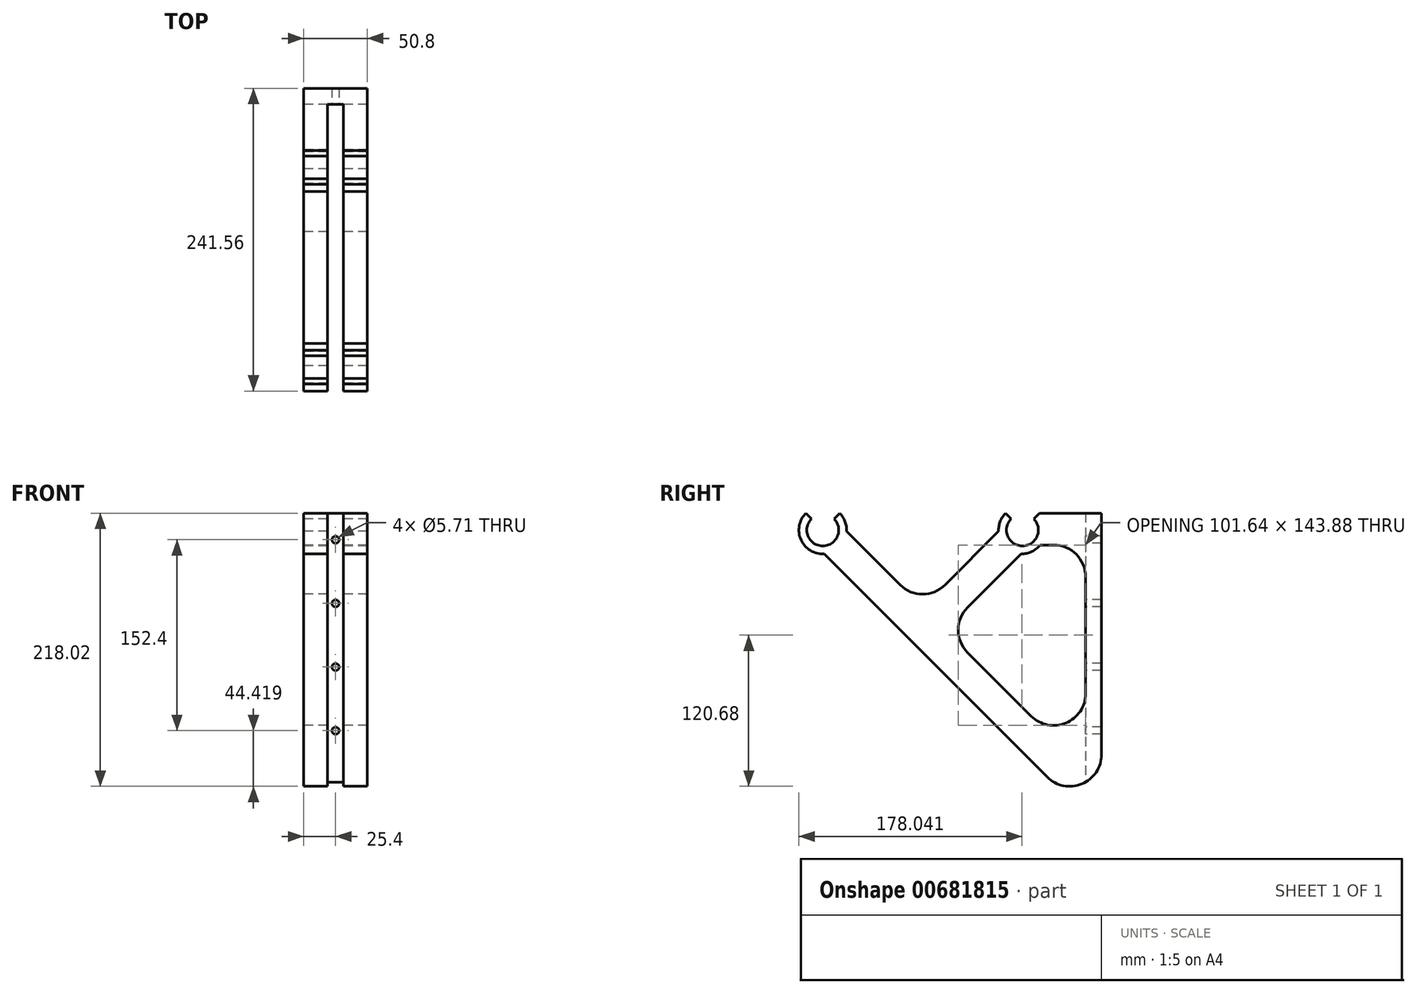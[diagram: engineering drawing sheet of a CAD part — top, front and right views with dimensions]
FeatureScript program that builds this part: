
annotation { "Feature Type Name" : "Feature", "Feature Type Description" : "" }
export const myFeature = defineFeature(function(context is Context, id is Id, definition is map)
    precondition{}
    {
        {
            var Q0;
            Q0=qCreatedBy(makeId("Right.planeOp"),FACE);
            var sketch = newSketch(context, id + "F0", { "sketchPlane" : qUnion([Q0])});
            skCircle(sketch, "E0", {"center": v(0, 0) * mm, "radius": 100 * mm});
            skLineSegment(sketch, "E1", {"start": v(0, 0) * mm, "end": v(0, -100) * mm});
            skLineSegment(sketch, "E2", {"start": v(0, 0) * mm, "end": v(70.71, -70.71) * mm});
            skLineSegment(sketch, "E3.MirrorCS", {"start": v(0, 0) * mm, "end": v(-70.71, -70.71) * mm});
            skCircle(sketch, "E4", {"center": v(79.7, -79.7) * mm, "radius": 12.7 * mm});
            skLineSegment(sketch, "E5", {"start": v(79.7, -79.7) * mm, "end": v(79.7, -67) * mm});
            skLineSegment(sketch, "E6", {"start": v(79.7, -79.7) * mm, "end": v(70.71, -70.71) * mm});
            skCircle(sketch, "E7.MirrorC", {"center": v(-79.7, -79.7) * mm, "radius": 12.7 * mm});
            skArc(sketch, "E8.0", {"start": v(-66.22, -66.22) * mm, "mid": v(-61.9, -72.9) * mm, "end": v(-60.67, -80.75) * mm});
            skLineSegment(sketch, "E9", {"start": v(-79.7, -79.7) * mm, "end": v(-79.7, -67) * mm});
            skLineSegment(sketch, "E10", {"start": v(-79.7, -79.7) * mm, "end": v(-93.16, -66.22) * mm});
            skLineSegment(sketch, "E11.MirrorCS", {"start": v(-79.7, -79.7) * mm, "end": v(-66.22, -66.22) * mm});
            skLineSegment(sketch, "E12.MirrorCS", {"start": v(79.7, -79.7) * mm, "end": v(66.22, -66.22) * mm});
            skLineSegment(sketch, "E13.MirrorCS", {"start": v(79.7, -79.7) * mm, "end": v(93.16, -66.22) * mm});
            skArc(sketch, "E14.trimOffspring", {"start": v(-79.7, -60.64) * mm, "mid": v(-79.6, -60.64) * mm, "end": v(-79.51, -60.64) * mm});
            skLineSegment(sketch, "E15", {"start": v(142.82, -66.22) * mm, "end": v(142.82, -258.84) * mm});
            skLineSegment(sketch, "E16.0", {"start": v(-78.63, -98.71) * mm, "end": v(99.46, -276.8) * mm});
            skLineSegment(sketch, "E17.0", {"start": v(-60.67, -80.75) * mm, "end": v(-17.96, -123.46) * mm});
            skLineSegment(sketch, "E18", {"start": v(142.82, -66.22) * mm, "end": v(130.12, -66.22) * mm});
            skLineSegment(sketch, "E19.0", {"start": v(93.89, -91.62) * mm, "end": v(104.72, -91.62) * mm});
            skLineSegment(sketch, "E20.0", {"start": v(78.63, -98.71) * mm, "end": v(35.92, -141.42) * mm});
            skLineSegment(sketch, "E21.0", {"start": v(60.67, -80.75) * mm, "end": v(17.96, -123.46) * mm});
            skArc(sketch, "E22.trimOffspring", {"start": v(60.67, -80.75) * mm, "mid": v(61.9, -72.9) * mm, "end": v(66.22, -66.22) * mm});
            skLineSegment(sketch, "E23.trimOffspring", {"start": v(35.92, -177.34) * mm, "end": v(86.76, -228.18) * mm});
            skArc(sketch, "E24.trimOffspring", {"start": v(-78.63, -98.71) * mm, "mid": v(-97.08, -87.47) * mm, "end": v(-93.16, -66.22) * mm});
            skArc(sketch, "E25.trimOffspring", {"start": v(93.89, -91.62) * mm, "mid": v(87.09, -96.94) * mm, "end": v(78.63, -98.71) * mm});
            skLineSegment(sketch, "E26.trimOffspring", {"start": v(130.12, -117.02) * mm, "end": v(130.12, -210.22) * mm});
            skLineSegment(sketch, "E27", {"start": v(93.16, -66.22) * mm, "end": v(130.12, -66.22) * mm});
            skPoint(sketch, "E28.visualSharp", {"position": v(0, -141.42) * mm});
            skArc(sketch, "E28.filletArc", {"start": v(-17.96, -123.46) * mm, "mid": v(0, -130.9) * mm, "end": v(17.96, -123.46) * mm});
            skPoint(sketch, "E29.visualSharp", {"position": v(17.96, -159.38) * mm});
            skArc(sketch, "E29.filletArc", {"start": v(35.92, -141.42) * mm, "mid": v(28.48, -159.38) * mm, "end": v(35.92, -177.34) * mm});
            skPoint(sketch, "E30.visualSharp", {"position": v(130.12, -91.62) * mm});
            skArc(sketch, "E30.filletArc", {"start": v(130.12, -117.02) * mm, "mid": v(122.68, -99.06) * mm, "end": v(104.72, -91.62) * mm});
            skPoint(sketch, "E31.visualSharp", {"position": v(130.12, -271.54) * mm});
            skArc(sketch, "E31.filletArc", {"start": v(86.76, -228.18) * mm, "mid": v(114.44, -233.69) * mm, "end": v(130.12, -210.22) * mm});
            skPoint(sketch, "E32.visualSharp", {"position": v(142.82, -320.16) * mm});
            skArc(sketch, "E32.filletArc", {"start": v(99.46, -276.8) * mm, "mid": v(127.14, -282.3) * mm, "end": v(142.82, -258.84) * mm});
            skSolve(sketch);
        }
        {
            var Q0;
            Q0=makeQuery(id+"F0.imprint","IMPRINT",FACE,{"disambiguationData":[TD([[makeQuery(id+"F0.imprint","IMPRINT",EDGE,{"derivedFrom":sQuery(id+"F0.wireOp",EDGE,"E15")}),-1.0]])]});
            var Q1;
            {var subQ0=sQuery(id+"F0.wireOp",EDGE,"E22.trimOffspring");var subQ1=sQuery(id+"F0.wireOp",EDGE,"E0");var subQ2=makeQuery(id+"F0.imprint","INTERSECT",VERTEX,{"derivedFrom":[subQ1,subQ0]});Q1=makeQuery(id+"F0.imprint","IMPRINT",FACE,{"disambiguationData":[TD([[makeQuery(id+"F0.imprint","IMPRINT",EDGE,{"disambiguationData":[TD([[subQ2,-1.0]])],"derivedFrom":subQ1}),1.0]])]});}
            var Q2;
            {var subQ0=sQuery(id+"F0.wireOp",EDGE,"E8.0");var subQ1=sQuery(id+"F0.wireOp",EDGE,"E0");var subQ2=makeQuery(id+"F0.imprint","INTERSECT",VERTEX,{"derivedFrom":[subQ1,subQ0]});Q2=makeQuery(id+"F0.imprint","IMPRINT",FACE,{"disambiguationData":[TD([[makeQuery(id+"F0.imprint","IMPRINT",EDGE,{"disambiguationData":[TD([[subQ2,1.0]])],"derivedFrom":subQ1}),1.0]])]});}
            extrude(context, id + "F1", {"entities" : qUnion([Q0, Q1, Q2]), "depth" : 50.8 * mm, "offsetDistance" : 25.4 * mm});
        }
        {
            var Q0;
            Q0=makeQuery(id+"F1.opExtrude","SWEPT_FACE",FACE,{"disambiguationData":[OSD([sQuery(id+"F0.wireOp",EDGE,"E26.trimOffspring")])]});
            cPlane(context, id + "F2", {"entities" : qUnion([Q0]), "cplaneType" : CPlaneType.OFFSET, "offset" : 254 * mm, "width" : 152.4 * mm, "height" : 152.4 * mm});
        }
        {
            var Q0;
            Q0=qCreatedBy(id+"F2.planeOp",FACE);
            var sketch = newSketch(context, id + "F3", { "sketchPlane" : qUnion([Q0])});
            skLineSegment(sketch, "E33.0", {"start": v(50.8, -66.22) * mm, "end": v(0, -66.22) * mm});
            skLineSegment(sketch, "E34", {"start": v(50.8, -284.24) * mm, "end": v(0, -284.24) * mm});
            skLineSegment(sketch, "E35", {"start": v(31.75, -66.22) * mm, "end": v(31.75, -284.24) * mm});
            skLineSegment(sketch, "E36", {"start": v(19.05, -66.22) * mm, "end": v(19.05, -284.24) * mm});
            skSolve(sketch);
        }
        {
            var Q0;
            Q0 = qSketchRegion(id + "F3", true);
            var Q1;
            Q1=makeQuery(id+"F1.opExtrude","SWEPT_FACE",FACE,{"disambiguationData":[OSD([sQuery(id+"F0.wireOp",EDGE,"E26.trimOffspring")])]});
            extrude(context, id + "F4", {"entities" : qUnion([Q0]), "operationType" : NewBodyOperationType.REMOVE, "endBound" : BoundingType.UP_TO_SURFACE, "oppositeDirection" : true, "depth" : 25.4 * mm, "endBoundEntityFace" : qUnion([Q1]), "offsetDistance" : 25.4 * mm});
        }
        {
            var Q0;
            {var subQ0=sQuery(id+"F0.wireOp",EDGE,"E26.trimOffspring");Q0=makeQuery(id+"F4.boolean.opBoolean","MERGE",FACE,{"derivedFrom":[makeQuery(id+"F1.opExtrude","SWEPT_FACE",FACE,{"disambiguationData":[OSD([subQ0])]}),makeQuery(id+"F4.opExtrude","CAP_FACE",FACE,{"disambiguationData":[OSD([subQ0])],"isStart":false})]});}
            var sketch = newSketch(context, id + "F5", { "sketchPlane" : qUnion([Q0])});
            skCircle(sketch, "E37", {"center": v(25.4, -138.22) * mm, "radius": 2.86 * mm});
            skPoint(sketch, "E37.centerSnap0", {"position": v(25.4, -66.22) * mm});
            skLineSegment(sketch, "E38", {"start": v(50.8, -163.62) * mm, "end": v(0, -163.62) * mm});
            skCircle(sketch, "E39.0.1.0", {"center": v(25.4, -87.42) * mm, "radius": 2.86 * mm});
            skLineSegment(sketch, "E39.direction1", {"start": v(25.4, -138.22) * mm, "end": v(50.8, -138.22) * mm, "construction": true});
            skLineSegment(sketch, "E39.direction2", {"start": v(25.4, -138.22) * mm, "end": v(25.4, -87.42) * mm, "construction": true});
            skCircle(sketch, "E40.MirrorC", {"center": v(25.4, -239.82) * mm, "radius": 2.86 * mm});
            skCircle(sketch, "E41.MirrorC", {"center": v(25.4, -189.02) * mm, "radius": 2.86 * mm});
            skSolve(sketch);
        }
        {
            var Q0;
            Q0 = qSketchRegion(id + "F5", true);
            extrude(context, id + "F6", {"entities" : qUnion([Q0]), "operationType" : NewBodyOperationType.REMOVE, "endBound" : BoundingType.THROUGH_ALL, "oppositeDirection" : true, "depth" : 25.4 * mm, "offsetDistance" : 25.4 * mm});
        }
    });
